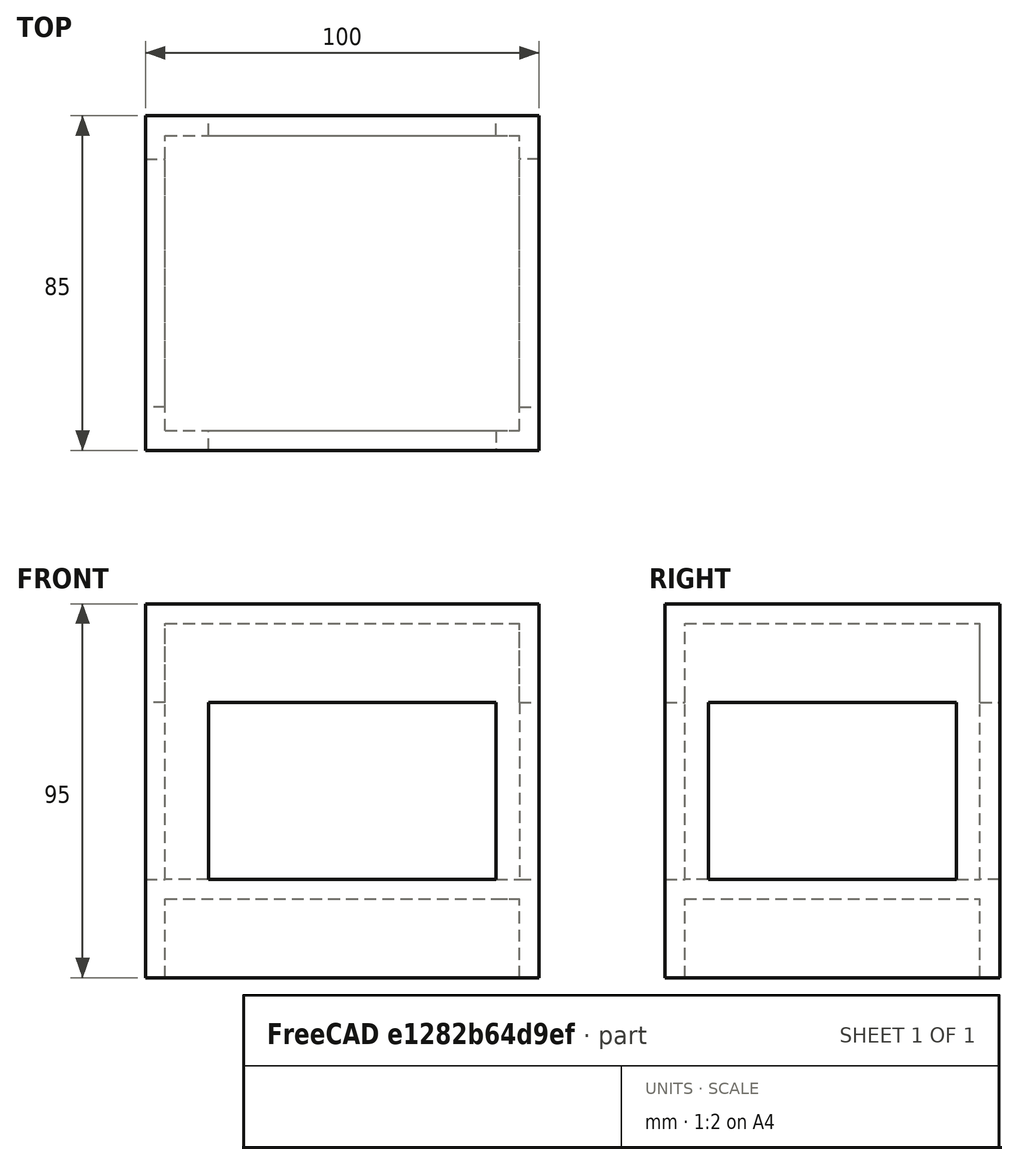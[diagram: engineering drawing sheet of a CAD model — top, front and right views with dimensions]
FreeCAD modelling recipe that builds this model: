
FCSTD DOCUMENT  (FreeCAD 0.16R6712 (Git))
Label: guarda placa
License: All rights reserved
LicenseURL: http://en.wikipedia.org/wiki/All_rights_reserved
objects: Part::Box×10, Part::MultiFuse×9, Part::Thickness×2
note: 21 computed .brp shape members not serialized (recipe doc carries the construction recipe); baked Part::Feature solids carry a one-line shape summary decoded from their .brp

FEATURE [Part::Box] Box  label="Planta2"
  Height = 20
  Length = 90
  Width = 75
FEATURE [Part::Box] Box001  label="Planta1"
  Height = 20
  Length = 90
  Placement = pos=(0,0,-50) rot=(0,0,1;0rad)
  Width = 75
FEATURE [Part::Thickness] Thickness
  Faces = -> Box001 [Face5]
  Intersection = true
  Join = 2
  Mode = 0
  Placement = pos=(0,0,-20) rot=(0,0,1;0rad)
  SelfIntersection = false
  Value = 5
FEATURE [Part::Thickness] Thickness001
  Faces = -> Box [Face5]
  Intersection = false
  Join = 2
  Mode = 0
  SelfIntersection = false
  Value = 5
FEATURE [Part::Box] Box002  label="pata01"
  Height = 50
  Length = 11
  Placement = pos=(0,-5,-49) rot=(0,0,1;1.5708rad)
  Width = 5
FEATURE [Part::Box] Box003  label="pata002"
  Height = 50
  Length = 11
  Placement = pos=(0,-5,-49) rot=(0,0,1;0rad)
  Width = 5
FEATURE [Part::Box] Box004  label="pata003"
  Height = 50
  Length = 11
  Placement = pos=(95,-5,-49) rot=(0,0,1;1.5708rad)
  Width = 5
FEATURE [Part::Box] Box005  label="pata004"
  Height = 50
  Length = 11
  Placement = pos=(84,-5,-49) rot=(0,0,1;0rad)
  Width = 5
FEATURE [Part::Box] Box006  label="pata005"
  Height = 50
  Length = 11
  Placement = pos=(0,69,-48) rot=(0,0,1;1.5708rad)
  Width = 5
FEATURE [Part::Box] Box007  label="pata006"
  Height = 50
  Length = 11
  Placement = pos=(0,75,-49) rot=(0,0,1;0rad)
  Width = 5
FEATURE [Part::Box] Box008  label="pata007"
  Height = 50
  Length = 11
  Placement = pos=(95,69,-50) rot=(0,0,1;1.5708rad)
  Width = 5
FEATURE [Part::Box] Box009  label="pata008"
  Height = 50
  Length = 11
  Placement = pos=(84,75,-50) rot=(0,0,1;0rad)
  Width = 5
FEATURE [Part::MultiFuse] Fusion
  Shapes = -> [Box007,Box009]
FEATURE [Part::MultiFuse] Fusion001
  Shapes = -> [Box002,Box003]
FEATURE [Part::MultiFuse] Fusion002
  Shapes = -> [Box004,Box005]
FEATURE [Part::MultiFuse] Fusion003
  Shapes = -> [Box006,Box008]
FEATURE [Part::MultiFuse] Fusion004
  Shapes = -> [Thickness001,Fusion]
FEATURE [Part::MultiFuse] Fusion005
  Shapes = -> [Thickness,Fusion001]
FEATURE [Part::MultiFuse] Fusion006
  Shapes = -> [Fusion002,Fusion003]
FEATURE [Part::MultiFuse] Fusion007
  Shapes = -> [Fusion004,Fusion005]
FEATURE [Part::MultiFuse] Fusion008
  Shapes = -> [Fusion006,Fusion007]
